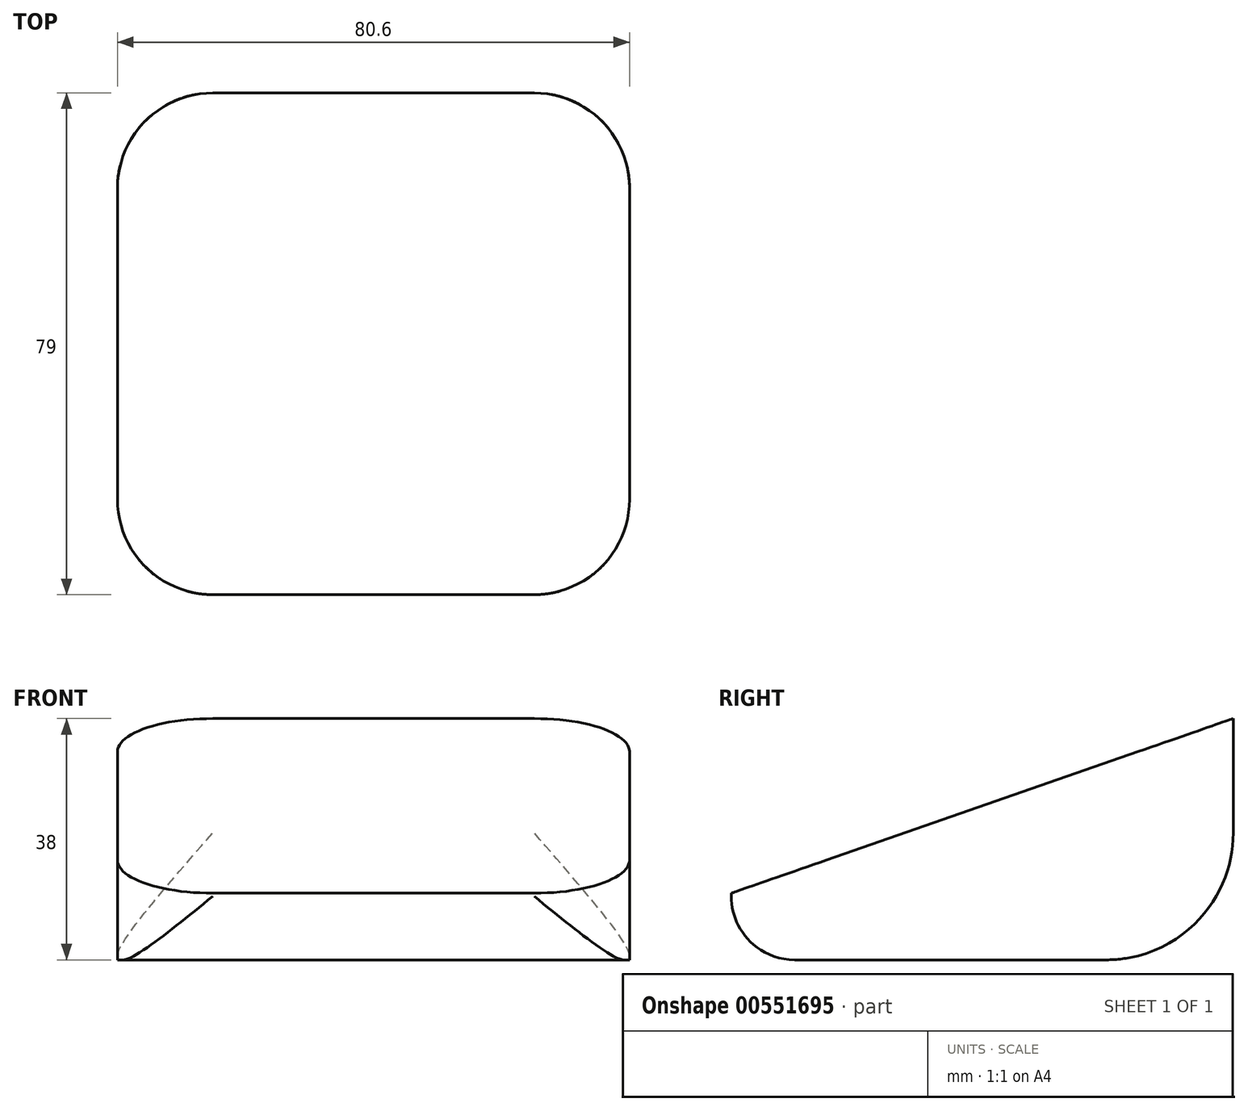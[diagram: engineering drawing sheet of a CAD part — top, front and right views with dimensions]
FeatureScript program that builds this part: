
annotation { "Feature Type Name" : "Feature", "Feature Type Description" : "" }
export const myFeature = defineFeature(function(context is Context, id is Id, definition is map)
    precondition{}
    {
        {
            var Q0;
            Q0=qCreatedBy(makeId("Right.planeOp"),FACE);
            var sketch = newSketch(context, id + "F0", { "sketchPlane" : qUnion([Q0])});
            skLineSegment(sketch, "E0", {"start": v(-39.5, 0) * mm, "end": v(39.5, 0) * mm});
            skLineSegment(sketch, "E1", {"start": v(39.5, 0) * mm, "end": v(39.5, 38) * mm});
            skLineSegment(sketch, "E2", {"start": v(39.5, 38) * mm, "end": v(-39.5, 10.5) * mm});
            skLineSegment(sketch, "E3", {"start": v(-39.5, 10.5) * mm, "end": v(-39.5, 0) * mm});
            skLineSegment(sketch, "E4", {"start": v(0, 0) * mm, "end": v(0, 18.48) * mm, "construction": true});
            skSolve(sketch);
        }
        {
            var Q0;
            Q0=qSketchRegion(id+"F0",true);
            extrude(context, id + "F1", {"entities" : qUnion([Q0]), "endBound" : BoundingType.SYMMETRIC, "depth" : 80.6 * mm});
        }
        {
            var Q0;
            Q0=makeQuery(id+"F1.opExtrude","CAP_EDGE",EDGE,{"disambiguationData":[OSD([sQuery(id+"F0.wireOp",EDGE,"E3")])],"isStart":false});
            var Q1;
            Q1=makeQuery(id+"F1.opExtrude","CAP_EDGE",EDGE,{"disambiguationData":[OSD([sQuery(id+"F0.wireOp",EDGE,"E1")])],"isStart":false});
            var Q2;
            Q2=makeQuery(id+"F1.opExtrude","CAP_EDGE",EDGE,{"disambiguationData":[OSD([sQuery(id+"F0.wireOp",EDGE,"E3")])],"isStart":true});
            var Q3;
            Q3=makeQuery(id+"F1.opExtrude","CAP_EDGE",EDGE,{"disambiguationData":[OSD([sQuery(id+"F0.wireOp",EDGE,"E1")])],"isStart":true});
            fillet(context, id + "F2", {"entities" : qUnion([Q0, Q1, Q2, Q3]), "radius" : 15 * mm, "tangentPropagation" : true, "allowEdgeOverflow" : false});
        }
        {
            var Q0;
            Q0=makeQuery(id+"F1.opExtrude","SWEPT_EDGE",EDGE,{"disambiguationData":[OSD([sQuery(id+"F0.wireOp",EDGE,"E0"),sQuery(id+"F0.wireOp",EDGE,"E1")])]});
            fillet(context, id + "F3", {"entities" : qUnion([Q0]), "radius" : 20 * mm, "allowEdgeOverflow" : false});
        }
        {
            var Q0;
            Q0=makeQuery(id+"F1.opExtrude","SWEPT_EDGE",EDGE,{"disambiguationData":[OSD([sQuery(id+"F0.wireOp",EDGE,"E0"),sQuery(id+"F0.wireOp",EDGE,"E3")])]});
            fillet(context, id + "F4", {"entities" : qUnion([Q0]), "radius" : 10 * mm, "allowEdgeOverflow" : false});
        }
    });
